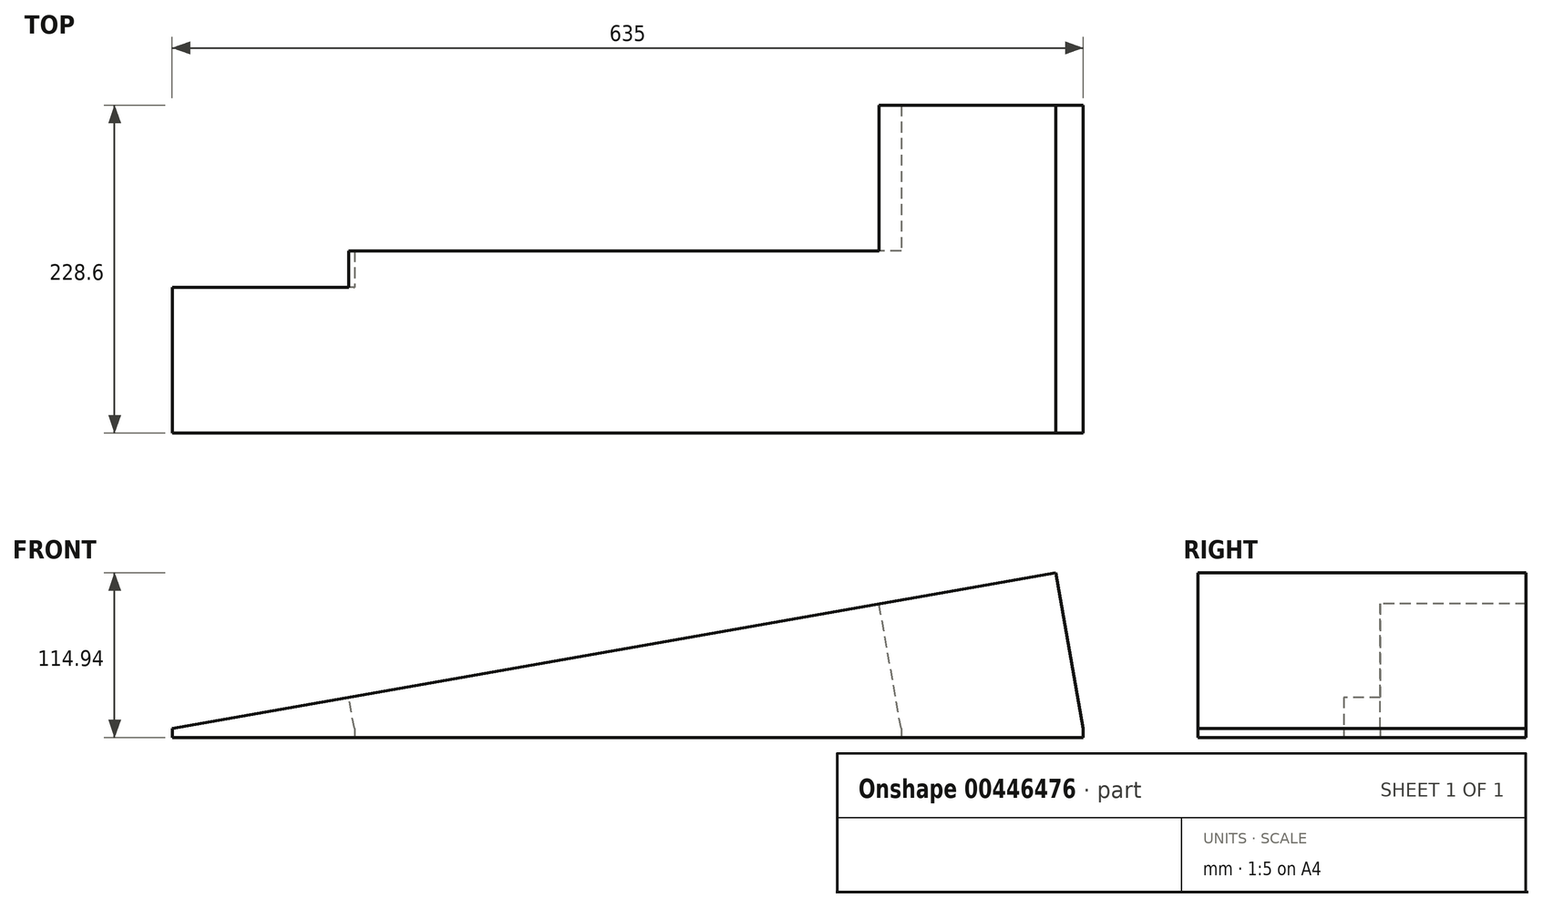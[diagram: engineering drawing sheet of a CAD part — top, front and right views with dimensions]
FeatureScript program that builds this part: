
annotation { "Feature Type Name" : "Feature", "Feature Type Description" : "" }
export const myFeature = defineFeature(function(context is Context, id is Id, definition is map)
    precondition{}
    {
        {
            var Q0;
            Q0=qCreatedBy(makeId("Top.planeOp"),FACE);
            var sketch = newSketch(context, id + "F0", { "sketchPlane" : qUnion([Q0])});
            skLineSegment(sketch, "E0", {"start": v(-165.09, 0) * mm, "end": v(469.91, 0) * mm});
            skLineSegment(sketch, "E1", {"start": v(469.91, 0) * mm, "end": v(469.91, 228.6) * mm});
            skLineSegment(sketch, "E2", {"start": v(469.91, 228.6) * mm, "end": v(342.91, 228.6) * mm});
            skLineSegment(sketch, "E3", {"start": v(342.91, 228.6) * mm, "end": v(342.91, 127) * mm});
            skLineSegment(sketch, "E4", {"start": v(342.91, 127) * mm, "end": v(-38.09, 127) * mm});
            skLineSegment(sketch, "E5", {"start": v(-165.09, 0) * mm, "end": v(-165.09, 101.6) * mm});
            skLineSegment(sketch, "E6", {"start": v(-165.09, 101.6) * mm, "end": v(-38.09, 101.6) * mm});
            skLineSegment(sketch, "E7", {"start": v(-38.09, 127) * mm, "end": v(-38.09, 101.6) * mm});
            skLineSegment(sketch, "E8.0", {"start": v(336.56, 133.35) * mm, "end": v(-35.66, 133.35) * mm});
            skLineSegment(sketch, "E8.1", {"start": v(336.56, 234.95) * mm, "end": v(336.56, 133.35) * mm});
            skLineSegment(sketch, "E8.2", {"start": v(476.26, 234.95) * mm, "end": v(336.56, 234.95) * mm});
            skLineSegment(sketch, "E8.3", {"start": v(-171.44, 107.95) * mm, "end": v(-44.44, 107.95) * mm});
            skLineSegment(sketch, "E8.4", {"start": v(-171.44, -6.35) * mm, "end": v(-171.44, 107.95) * mm});
            skLineSegment(sketch, "E8.5", {"start": v(-171.44, -6.35) * mm, "end": v(476.26, -6.35) * mm});
            skLineSegment(sketch, "E8.6", {"start": v(476.26, -6.35) * mm, "end": v(476.26, 234.95) * mm});
            skLineSegment(sketch, "E9.0", {"start": v(-44.44, 126.55) * mm, "end": v(-44.44, 107.95) * mm});
            skLineSegment(sketch, "E10", {"start": v(-35.66, 133.35) * mm, "end": v(-44.44, 133.35) * mm});
            skLineSegment(sketch, "E11", {"start": v(-44.44, 133.35) * mm, "end": v(-44.44, 126.55) * mm});
            skSolve(sketch);
        }
        {
            var Q0;
            Q0=makeQuery(id+"F0.imprint","IMPRINT",FACE,{"disambiguationData":[TD([[makeQuery(id+"F0.imprint","IMPRINT",EDGE,{"derivedFrom":sQuery(id+"F0.wireOp",EDGE,"E0")}),1.0]])]});
            extrude(context, id + "F1", {"entities" : qUnion([Q0]), "depth" : 6.35 * mm});
        }
        {
            var Q0;
            Q0=makeQuery(id+"F1.opExtrude","CAP_EDGE",EDGE,{"disambiguationData":[OSD([sQuery(id+"F0.wireOp",EDGE,"E5")])],"isStart":false});
            var Q1;
            Q1=makeQuery(id+"F1.opExtrude","CAP_FACE",FACE,{"disambiguationData":[OSD([sQuery(id+"F0.wireOp",EDGE,"E0"),sQuery(id+"F0.wireOp",EDGE,"E1"),sQuery(id+"F0.wireOp",EDGE,"E2"),sQuery(id+"F0.wireOp",EDGE,"E3"),sQuery(id+"F0.wireOp",EDGE,"E4"),sQuery(id+"F0.wireOp",EDGE,"E5"),sQuery(id+"F0.wireOp",EDGE,"E6"),sQuery(id+"F0.wireOp",EDGE,"E7")])],"isStart":false});
            cPlane(context, id + "F2", {"entities" : qUnion([Q0, Q1]), "cplaneType" : CPlaneType.LINE_ANGLE, "offset" : 25.4 * mm, "angle" : 350 * degree, "width" : 152.4 * mm, "height" : 152.4 * mm});
        }
        {
            var Q0;
            Q0=qCreatedBy(id+"F2.planeOp",FACE);
            var sketch = newSketch(context, id + "F3", { "sketchPlane" : qUnion([Q0])});
            skLineSegment(sketch, "E12.0.0", {"start": v(338.8, -127) * mm, "end": v(-36.4, -127) * mm});
            skLineSegment(sketch, "E12.0.1", {"start": v(-36.4, -127) * mm, "end": v(-36.4, -101.6) * mm});
            skLineSegment(sketch, "E12.0.2", {"start": v(-36.4, -101.6) * mm, "end": v(-161.48, -101.6) * mm});
            skLineSegment(sketch, "E12.0.3", {"start": v(-161.48, -101.6) * mm, "end": v(-161.48, 0) * mm});
            skLineSegment(sketch, "E12.0.4", {"start": v(-161.48, 0) * mm, "end": v(463.88, 0) * mm});
            skLineSegment(sketch, "E12.0.5", {"start": v(463.88, 0) * mm, "end": v(463.88, -228.6) * mm});
            skLineSegment(sketch, "E12.0.6", {"start": v(463.88, -228.6) * mm, "end": v(338.8, -228.6) * mm});
            skLineSegment(sketch, "E12.0.7", {"start": v(338.8, -228.6) * mm, "end": v(338.8, -127) * mm});
            skSolve(sketch);
        }
        {
            var Q0;
            Q0=makeQuery(id+"F3.imprint","IMPRINT",FACE,{"disambiguationData":[TD([[makeQuery(id+"F3.imprint","IMPRINT",EDGE,{"derivedFrom":sQuery(id+"F3.wireOp",EDGE,"E12.0.0")}),-1.0]])]});
            extrude(context, id + "F4", {"entities" : qUnion([Q0]), "operationType" : NewBodyOperationType.ADD, "endBound" : BoundingType.UP_TO_NEXT, "depth" : 25.4 * mm});
        }
    });
